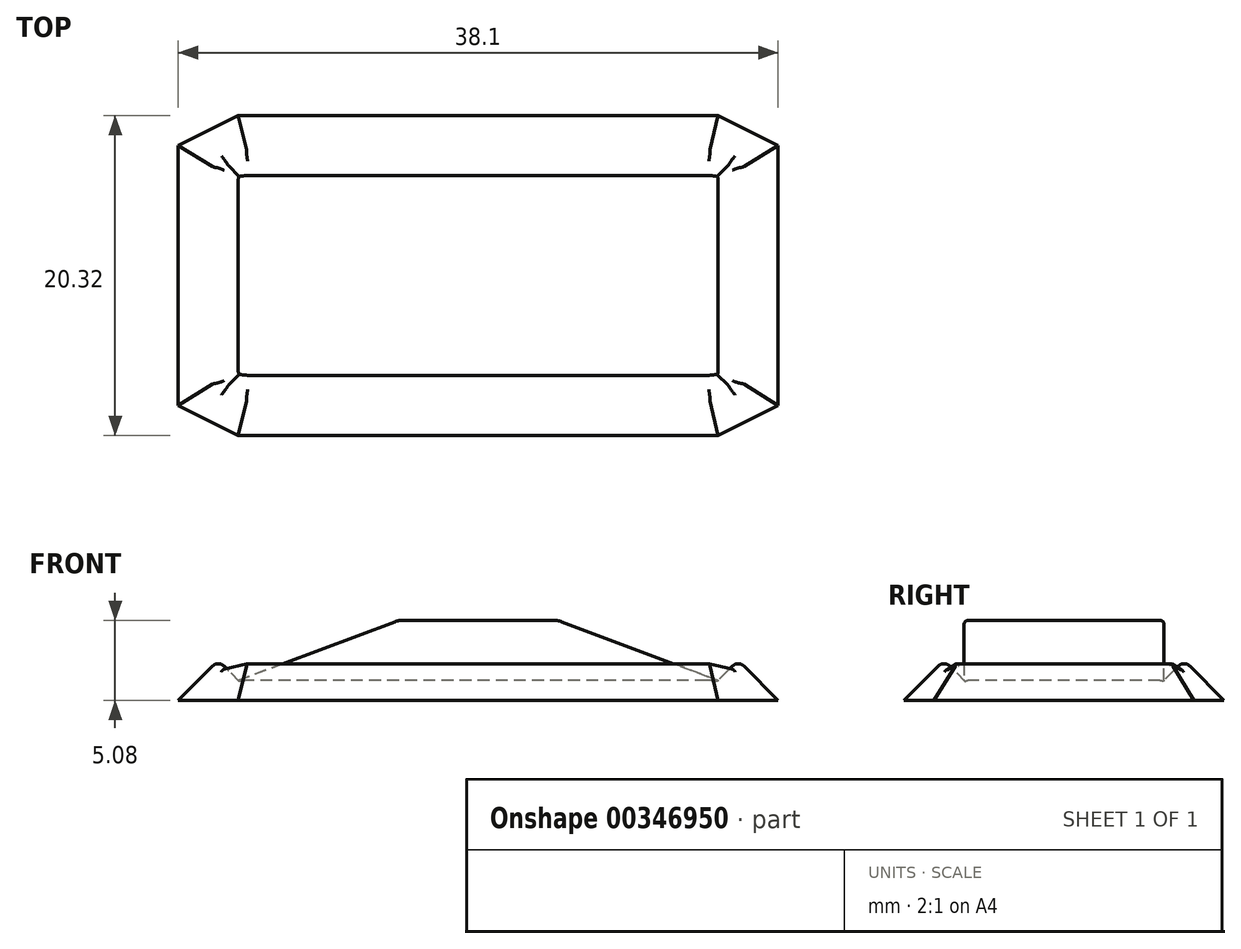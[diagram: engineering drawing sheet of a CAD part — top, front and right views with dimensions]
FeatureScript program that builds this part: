
annotation { "Feature Type Name" : "Feature", "Feature Type Description" : "" }
export const myFeature = defineFeature(function(context is Context, id is Id, definition is map)
    precondition{}
    {
        {
            var Q0;
            Q0=qCreatedBy(makeId("Top.planeOp"),FACE);
            var sketch = newSketch(context, id + "F0", { "sketchPlane" : qUnion([Q0])});
            skLineSegment(sketch, "E0.bottom", {"start": v(-41.99, -20.24) * mm, "end": v(-11.5, -20.24) * mm});
            skLineSegment(sketch, "E0.top", {"start": v(-41.99, -32.94) * mm, "end": v(-11.5, -32.94) * mm});
            skLineSegment(sketch, "E0.left", {"start": v(-41.99, -20.24) * mm, "end": v(-41.99, -32.94) * mm});
            skLineSegment(sketch, "E0.right", {"start": v(-11.5, -20.24) * mm, "end": v(-11.5, -32.94) * mm});
            skLineSegment(sketch, "E1.0", {"start": v(-41.99, -16.43) * mm, "end": v(-11.5, -16.43) * mm});
            skLineSegment(sketch, "E2.0", {"start": v(-41.99, -36.75) * mm, "end": v(-11.5, -36.75) * mm});
            skLineSegment(sketch, "E3.0", {"start": v(-6.43, -18.97) * mm, "end": v(-6.43, -34.2) * mm});
            skLineSegment(sketch, "E4.0", {"start": v(-47.07, -18.97) * mm, "end": v(-47.07, -34.2) * mm});
            skLineSegment(sketch, "E5", {"start": v(-47.07, -18.97) * mm, "end": v(-41.99, -16.43) * mm});
            skLineSegment(sketch, "E6", {"start": v(-11.5, -16.43) * mm, "end": v(-6.43, -18.97) * mm});
            skLineSegment(sketch, "E7", {"start": v(-6.43, -34.2) * mm, "end": v(-11.5, -36.75) * mm});
            skLineSegment(sketch, "E8", {"start": v(-41.99, -36.75) * mm, "end": v(-47.07, -34.2) * mm});
            skSolve(sketch);
        }
        {
            var Q0;
            Q0=makeQuery(id+"F0.imprint","IMPRINT",FACE,{"disambiguationData":[TD([[makeQuery(id+"F0.imprint","IMPRINT",EDGE,{"derivedFrom":sQuery(id+"F0.wireOp",EDGE,"E0.bottom")}),1.0]])]});
            extrude(context, id + "F1", {"entities" : qUnion([Q0]), "depth" : 2.54 * mm});
        }
        {
            var Q0;
            Q0=makeQuery(id+"F1.opExtrude","CAP_EDGE",EDGE,{"disambiguationData":[OSD([sQuery(id+"F0.wireOp",EDGE,"E4.0")])],"isStart":false});
            var Q1;
            Q1=makeQuery(id+"F1.opExtrude","CAP_EDGE",EDGE,{"disambiguationData":[OSD([sQuery(id+"F0.wireOp",EDGE,"E3.0")])],"isStart":false});
            chamfer(context, id + "F2", {"entities" : qUnion([Q0, Q1]), "width" : 3.8 * mm, "tangentPropagation" : true});
        }
        {
            var Q0;
            Q0=makeQuery(id+"F1.opExtrude","CAP_EDGE",EDGE,{"disambiguationData":[OSD([sQuery(id+"F0.wireOp",EDGE,"E8")])],"isStart":false});
            var Q1;
            Q1=makeQuery(id+"F1.opExtrude","CAP_EDGE",EDGE,{"disambiguationData":[OSD([sQuery(id+"F0.wireOp",EDGE,"E5")])],"isStart":false});
            var Q2;
            Q2=makeQuery(id+"F1.opExtrude","CAP_EDGE",EDGE,{"disambiguationData":[OSD([sQuery(id+"F0.wireOp",EDGE,"E6")])],"isStart":false});
            var Q3;
            Q3=makeQuery(id+"F1.opExtrude","CAP_EDGE",EDGE,{"disambiguationData":[OSD([sQuery(id+"F0.wireOp",EDGE,"E7")])],"isStart":false});
            chamfer(context, id + "F3", {"entities" : qUnion([Q0, Q1, Q2, Q3]), "width" : 2.54 * mm, "tangentPropagation" : true});
        }
        {
            var Q0;
            Q0=makeQuery(id+"F1.opExtrude","CAP_EDGE",EDGE,{"disambiguationData":[OSD([sQuery(id+"F0.wireOp",EDGE,"E2.0")])],"isStart":false});
            var Q1;
            Q1=makeQuery(id+"F1.opExtrude","CAP_EDGE",EDGE,{"disambiguationData":[OSD([sQuery(id+"F0.wireOp",EDGE,"E1.0")])],"isStart":false});
            chamfer(context, id + "F4", {"entities" : qUnion([Q0, Q1]), "width" : 2.54 * mm, "tangentPropagation" : true});
        }
        {
            var Q0;
            Q0=makeQuery(id+"F1.opExtrude","CAP_EDGE",EDGE,{"disambiguationData":[OSD([sQuery(id+"F0.wireOp",EDGE,"E0.bottom")])],"isStart":false});
            var Q1;
            Q1=makeQuery(id+"F1.opExtrude","CAP_EDGE",EDGE,{"disambiguationData":[OSD([sQuery(id+"F0.wireOp",EDGE,"E0.left")])],"isStart":false});
            var Q2;
            Q2=makeQuery(id+"F1.opExtrude","CAP_EDGE",EDGE,{"disambiguationData":[OSD([sQuery(id+"F0.wireOp",EDGE,"E0.top")])],"isStart":false});
            var Q3;
            Q3=makeQuery(id+"F1.opExtrude","CAP_EDGE",EDGE,{"disambiguationData":[OSD([sQuery(id+"F0.wireOp",EDGE,"E0.right")])],"isStart":false});
            chamfer(context, id + "F5", {"entities" : qUnion([Q0, Q1, Q2, Q3]), "width" : 1.27 * mm, "tangentPropagation" : true});
        }
        {
            var Q0;
            Q0=makeQuery(id+"F0.imprint","IMPRINT",FACE,{"disambiguationData":[TD([[makeQuery(id+"F0.imprint","IMPRINT",EDGE,{"derivedFrom":sQuery(id+"F0.wireOp",EDGE,"E0.bottom")}),-1.0]])]});
            extrude(context, id + "F6", {"entities" : qUnion([Q0]), "operationType" : NewBodyOperationType.ADD, "depth" : 5.08 * mm});
        }
        {
            var Q0;
            Q0=makeQuery(id+"F6.opExtrude","CAP_EDGE",EDGE,{"disambiguationData":[OSD([sQuery(id+"F0.wireOp",EDGE,"E0.left")])],"isStart":false});
            var Q1;
            Q1=makeQuery(id+"F6.opExtrude","CAP_EDGE",EDGE,{"disambiguationData":[OSD([sQuery(id+"F0.wireOp",EDGE,"E0.right")])],"isStart":false});
            chamfer(context, id + "F7", {"entities" : qUnion([Q0, Q1]), "chamferType" : ChamferType.TWO_OFFSETS, "width1" : 10.16 * mm, "oppositeDirection" : false, "width2" : 3.8 * mm, "tangentPropagation" : true});
        }
        {
            var Q0;
            Q0=makeQuery(id+"F6.opExtrude","CAP_EDGE",EDGE,{"disambiguationData":[OSD([sQuery(id+"F0.wireOp",EDGE,"E0.top")])],"isStart":false});
            var Q1;
            Q1=makeQuery(id+"F7.opChamfer","BLEND_EDGE",EDGE,{"blendedFrom":[makeQuery(id+"F6.opExtrude","CAP_EDGE",EDGE,{"disambiguationData":[OSD([sQuery(id+"F0.wireOp",EDGE,"E0.right")])],"isStart":false}),makeQuery(id+"F6.opExtrude","SWEPT_FACE",FACE,{"disambiguationData":[OSD([sQuery(id+"F0.wireOp",EDGE,"E0.top")])]})],"blendedInto":[makeQuery(id+"F6.opExtrude","SWEPT_FACE",FACE,{"disambiguationData":[OSD([sQuery(id+"F0.wireOp",EDGE,"E0.top")])]})]});
            var Q2;
            Q2=makeQuery(id+"F7.opChamfer","BLEND_EDGE",EDGE,{"blendedFrom":[makeQuery(id+"F6.opExtrude","CAP_EDGE",EDGE,{"disambiguationData":[OSD([sQuery(id+"F0.wireOp",EDGE,"E0.left")])],"isStart":false}),makeQuery(id+"F6.opExtrude","SWEPT_FACE",FACE,{"disambiguationData":[OSD([sQuery(id+"F0.wireOp",EDGE,"E0.top")])]})],"blendedInto":[makeQuery(id+"F6.opExtrude","SWEPT_FACE",FACE,{"disambiguationData":[OSD([sQuery(id+"F0.wireOp",EDGE,"E0.top")])]})]});
            var Q3;
            Q3=makeQuery(id+"F7.opChamfer","BLEND_EDGE",EDGE,{"blendedFrom":[makeQuery(id+"F6.opExtrude","CAP_EDGE",EDGE,{"disambiguationData":[OSD([sQuery(id+"F0.wireOp",EDGE,"E0.left")])],"isStart":false}),makeQuery(id+"F6.opExtrude","SWEPT_FACE",FACE,{"disambiguationData":[OSD([sQuery(id+"F0.wireOp",EDGE,"E0.bottom")])]})],"blendedInto":[makeQuery(id+"F6.opExtrude","SWEPT_FACE",FACE,{"disambiguationData":[OSD([sQuery(id+"F0.wireOp",EDGE,"E0.bottom")])]})]});
            var Q4;
            Q4=makeQuery(id+"F6.opExtrude","CAP_EDGE",EDGE,{"disambiguationData":[OSD([sQuery(id+"F0.wireOp",EDGE,"E0.bottom")])],"isStart":false});
            var Q5;
            Q5=makeQuery(id+"F7.opChamfer","BLEND_EDGE",EDGE,{"blendedFrom":[makeQuery(id+"F6.opExtrude","CAP_EDGE",EDGE,{"disambiguationData":[OSD([sQuery(id+"F0.wireOp",EDGE,"E0.right")])],"isStart":false}),makeQuery(id+"F6.opExtrude","SWEPT_FACE",FACE,{"disambiguationData":[OSD([sQuery(id+"F0.wireOp",EDGE,"E0.bottom")])]})],"blendedInto":[makeQuery(id+"F6.opExtrude","SWEPT_FACE",FACE,{"disambiguationData":[OSD([sQuery(id+"F0.wireOp",EDGE,"E0.bottom")])]})]});
            fillet(context, id + "F8", {"entities" : qUnion([Q0, Q1, Q2, Q3, Q4, Q5]), "radius" : 0.25 * mm, "tangentPropagation" : true, "allowEdgeOverflow" : false});
        }
        {
            var Q0;
            {var subQ0=sQuery(id+"F0.wireOp",EDGE,"E0.left");Q0=makeQuery(id+"F7.opChamfer","BLEND_EDGE",EDGE,{"blendedFrom":[makeQuery(id+"F6.opExtrude","CAP_EDGE",EDGE,{"disambiguationData":[OSD([subQ0])],"isStart":false}),makeQuery(id+"F6.opExtrude","CAP_FACE",FACE,{"disambiguationData":[OSD([sQuery(id+"F0.wireOp",EDGE,"E0.bottom"),sQuery(id+"F0.wireOp",EDGE,"E0.top"),subQ0,sQuery(id+"F0.wireOp",EDGE,"E0.right")])],"isStart":false})],"blendedInto":[makeQuery(id+"F6.opExtrude","CAP_FACE",FACE,{"disambiguationData":[OSD([sQuery(id+"F0.wireOp",EDGE,"E0.bottom"),sQuery(id+"F0.wireOp",EDGE,"E0.top"),subQ0,sQuery(id+"F0.wireOp",EDGE,"E0.right")])],"isStart":false})]});}
            var Q1;
            {var subQ0=sQuery(id+"F0.wireOp",EDGE,"E0.right");Q1=makeQuery(id+"F7.opChamfer","BLEND_EDGE",EDGE,{"blendedFrom":[makeQuery(id+"F6.opExtrude","CAP_EDGE",EDGE,{"disambiguationData":[OSD([subQ0])],"isStart":false}),makeQuery(id+"F6.opExtrude","CAP_FACE",FACE,{"disambiguationData":[OSD([sQuery(id+"F0.wireOp",EDGE,"E0.bottom"),sQuery(id+"F0.wireOp",EDGE,"E0.top"),sQuery(id+"F0.wireOp",EDGE,"E0.left"),subQ0])],"isStart":false})],"blendedInto":[makeQuery(id+"F6.opExtrude","CAP_FACE",FACE,{"disambiguationData":[OSD([sQuery(id+"F0.wireOp",EDGE,"E0.bottom"),sQuery(id+"F0.wireOp",EDGE,"E0.top"),sQuery(id+"F0.wireOp",EDGE,"E0.left"),subQ0])],"isStart":false})]});}
            fillet(context, id + "F9", {"entities" : qUnion([Q0, Q1]), "radius" : 1.27 * mm, "tangentPropagation" : true, "allowEdgeOverflow" : false});
        }
        {
            var Q0;
            Q0=makeQuery(id+"F5.opChamfer","BLEND_EDGE",EDGE,{"blendedFrom":[makeQuery(id+"F1.opExtrude","CAP_EDGE",EDGE,{"disambiguationData":[OSD([sQuery(id+"F0.wireOp",EDGE,"E0.left")])],"isStart":false}),makeQuery(id+"F2.opChamfer","BLEND_FACE",FACE,{"disambiguationData":[OSD([sQuery(id+"F0.wireOp",EDGE,"E4.0")])]})],"blendedInto":[makeQuery(id+"F2.opChamfer","BLEND_FACE",FACE,{"disambiguationData":[OSD([sQuery(id+"F0.wireOp",EDGE,"E4.0")])]})]});
            var Q1;
            Q1=makeQuery(id+"F5.opChamfer","BLEND_EDGE",EDGE,{"blendedFrom":[makeQuery(id+"F1.opExtrude","CAP_EDGE",EDGE,{"disambiguationData":[OSD([sQuery(id+"F0.wireOp",EDGE,"E0.left")])],"isStart":false}),makeQuery(id+"F3.opChamfer","BLEND_FACE",FACE,{"disambiguationData":[OSD([sQuery(id+"F0.wireOp",EDGE,"E5")])]})],"blendedInto":[makeQuery(id+"F3.opChamfer","BLEND_FACE",FACE,{"disambiguationData":[OSD([sQuery(id+"F0.wireOp",EDGE,"E5")])]})]});
            var Q2;
            Q2=makeQuery(id+"F5.opChamfer","BLEND_EDGE",EDGE,{"blendedFrom":[makeQuery(id+"F1.opExtrude","CAP_EDGE",EDGE,{"disambiguationData":[OSD([sQuery(id+"F0.wireOp",EDGE,"E0.bottom")])],"isStart":false}),makeQuery(id+"F3.opChamfer","BLEND_FACE",FACE,{"disambiguationData":[OSD([sQuery(id+"F0.wireOp",EDGE,"E5")])]})],"blendedInto":[makeQuery(id+"F3.opChamfer","BLEND_FACE",FACE,{"disambiguationData":[OSD([sQuery(id+"F0.wireOp",EDGE,"E5")])]})]});
            var Q3;
            Q3=makeQuery(id+"F5.opChamfer","BLEND_EDGE",EDGE,{"blendedFrom":[makeQuery(id+"F1.opExtrude","CAP_EDGE",EDGE,{"disambiguationData":[OSD([sQuery(id+"F0.wireOp",EDGE,"E0.bottom")])],"isStart":false}),makeQuery(id+"F4.opChamfer","BLEND_FACE",FACE,{"disambiguationData":[OSD([sQuery(id+"F0.wireOp",EDGE,"E1.0")])]})],"blendedInto":[makeQuery(id+"F4.opChamfer","BLEND_FACE",FACE,{"disambiguationData":[OSD([sQuery(id+"F0.wireOp",EDGE,"E1.0")])]})]});
            var Q4;
            Q4=makeQuery(id+"F5.opChamfer","BLEND_EDGE",EDGE,{"blendedFrom":[makeQuery(id+"F1.opExtrude","CAP_EDGE",EDGE,{"disambiguationData":[OSD([sQuery(id+"F0.wireOp",EDGE,"E0.bottom")])],"isStart":false}),makeQuery(id+"F3.opChamfer","BLEND_FACE",FACE,{"disambiguationData":[OSD([sQuery(id+"F0.wireOp",EDGE,"E6")])]})],"blendedInto":[makeQuery(id+"F3.opChamfer","BLEND_FACE",FACE,{"disambiguationData":[OSD([sQuery(id+"F0.wireOp",EDGE,"E6")])]})]});
            var Q5;
            Q5=makeQuery(id+"F5.opChamfer","BLEND_EDGE",EDGE,{"blendedFrom":[makeQuery(id+"F1.opExtrude","CAP_EDGE",EDGE,{"disambiguationData":[OSD([sQuery(id+"F0.wireOp",EDGE,"E0.right")])],"isStart":false}),makeQuery(id+"F3.opChamfer","BLEND_FACE",FACE,{"disambiguationData":[OSD([sQuery(id+"F0.wireOp",EDGE,"E6")])]})],"blendedInto":[makeQuery(id+"F3.opChamfer","BLEND_FACE",FACE,{"disambiguationData":[OSD([sQuery(id+"F0.wireOp",EDGE,"E6")])]})]});
            var Q6;
            Q6=makeQuery(id+"F5.opChamfer","BLEND_EDGE",EDGE,{"blendedFrom":[makeQuery(id+"F1.opExtrude","CAP_EDGE",EDGE,{"disambiguationData":[OSD([sQuery(id+"F0.wireOp",EDGE,"E0.right")])],"isStart":false}),makeQuery(id+"F2.opChamfer","BLEND_FACE",FACE,{"disambiguationData":[OSD([sQuery(id+"F0.wireOp",EDGE,"E3.0")])]})],"blendedInto":[makeQuery(id+"F2.opChamfer","BLEND_FACE",FACE,{"disambiguationData":[OSD([sQuery(id+"F0.wireOp",EDGE,"E3.0")])]})]});
            var Q7;
            Q7=makeQuery(id+"F5.opChamfer","BLEND_EDGE",EDGE,{"blendedFrom":[makeQuery(id+"F1.opExtrude","CAP_EDGE",EDGE,{"disambiguationData":[OSD([sQuery(id+"F0.wireOp",EDGE,"E0.top")])],"isStart":false}),makeQuery(id+"F3.opChamfer","BLEND_FACE",FACE,{"disambiguationData":[OSD([sQuery(id+"F0.wireOp",EDGE,"E7")])]})],"blendedInto":[makeQuery(id+"F3.opChamfer","BLEND_FACE",FACE,{"disambiguationData":[OSD([sQuery(id+"F0.wireOp",EDGE,"E7")])]})]});
            var Q8;
            Q8=makeQuery(id+"F5.opChamfer","BLEND_EDGE",EDGE,{"blendedFrom":[makeQuery(id+"F1.opExtrude","CAP_EDGE",EDGE,{"disambiguationData":[OSD([sQuery(id+"F0.wireOp",EDGE,"E0.right")])],"isStart":false}),makeQuery(id+"F3.opChamfer","BLEND_FACE",FACE,{"disambiguationData":[OSD([sQuery(id+"F0.wireOp",EDGE,"E7")])]})],"blendedInto":[makeQuery(id+"F3.opChamfer","BLEND_FACE",FACE,{"disambiguationData":[OSD([sQuery(id+"F0.wireOp",EDGE,"E7")])]})]});
            var Q9;
            Q9=makeQuery(id+"F5.opChamfer","BLEND_EDGE",EDGE,{"blendedFrom":[makeQuery(id+"F1.opExtrude","CAP_EDGE",EDGE,{"disambiguationData":[OSD([sQuery(id+"F0.wireOp",EDGE,"E0.top")])],"isStart":false}),makeQuery(id+"F4.opChamfer","BLEND_FACE",FACE,{"disambiguationData":[OSD([sQuery(id+"F0.wireOp",EDGE,"E2.0")])]})],"blendedInto":[makeQuery(id+"F4.opChamfer","BLEND_FACE",FACE,{"disambiguationData":[OSD([sQuery(id+"F0.wireOp",EDGE,"E2.0")])]})]});
            var Q10;
            Q10=makeQuery(id+"F5.opChamfer","BLEND_EDGE",EDGE,{"blendedFrom":[makeQuery(id+"F1.opExtrude","CAP_EDGE",EDGE,{"disambiguationData":[OSD([sQuery(id+"F0.wireOp",EDGE,"E0.left")])],"isStart":false}),makeQuery(id+"F3.opChamfer","BLEND_FACE",FACE,{"disambiguationData":[OSD([sQuery(id+"F0.wireOp",EDGE,"E8")])]})],"blendedInto":[makeQuery(id+"F3.opChamfer","BLEND_FACE",FACE,{"disambiguationData":[OSD([sQuery(id+"F0.wireOp",EDGE,"E8")])]})]});
            var Q11;
            Q11=makeQuery(id+"F5.opChamfer","BLEND_EDGE",EDGE,{"blendedFrom":[makeQuery(id+"F1.opExtrude","CAP_EDGE",EDGE,{"disambiguationData":[OSD([sQuery(id+"F0.wireOp",EDGE,"E0.top")])],"isStart":false}),makeQuery(id+"F3.opChamfer","BLEND_FACE",FACE,{"disambiguationData":[OSD([sQuery(id+"F0.wireOp",EDGE,"E8")])]})],"blendedInto":[makeQuery(id+"F3.opChamfer","BLEND_FACE",FACE,{"disambiguationData":[OSD([sQuery(id+"F0.wireOp",EDGE,"E8")])]})]});
            fillet(context, id + "F10", {"entities" : qUnion([Q0, Q1, Q2, Q3, Q4, Q5, Q6, Q7, Q8, Q9, Q10, Q11]), "radius" : 0.5 * mm, "tangentPropagation" : true, "allowEdgeOverflow" : false});
        }
    });
